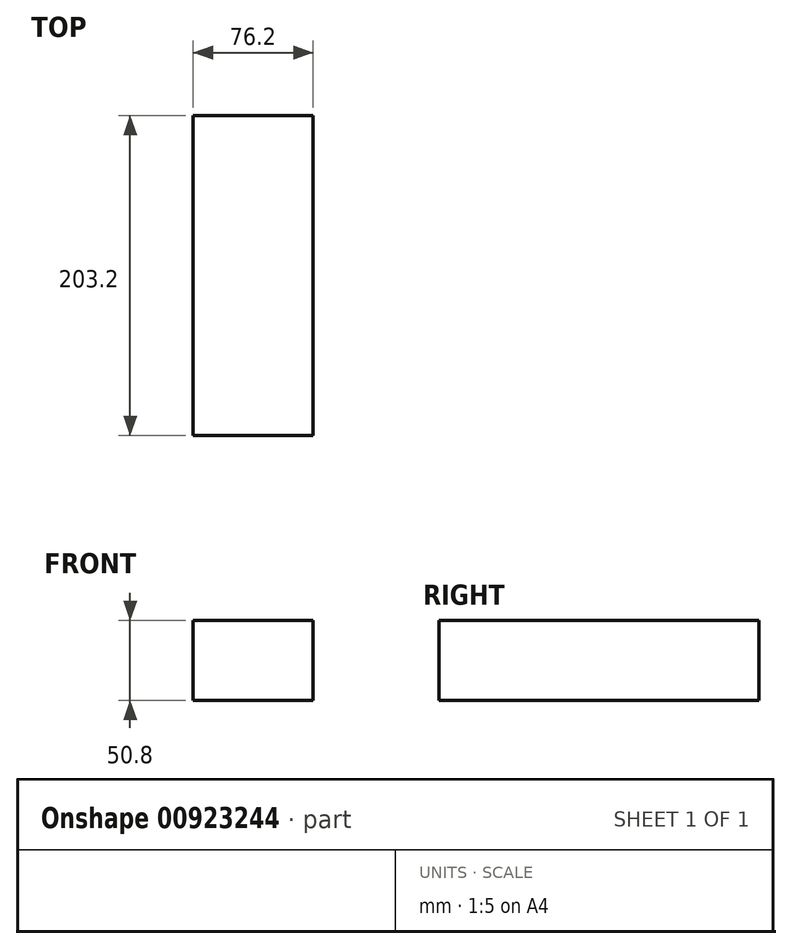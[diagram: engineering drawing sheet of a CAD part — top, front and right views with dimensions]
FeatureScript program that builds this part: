
annotation { "Feature Type Name" : "Feature", "Feature Type Description" : "" }
export const myFeature = defineFeature(function(context is Context, id is Id, definition is map)
    precondition{}
    {
        {
            var Q0;
            Q0=qCreatedBy(makeId("Top.planeOp"),FACE);
            var sketch = newSketch(context, id + "F0", { "sketchPlane" : qUnion([Q0])});
            skLineSegment(sketch, "E0.bottom", {"start": v(0, 0) * mm, "end": v(76.2, 0) * mm});
            skLineSegment(sketch, "E0.top", {"start": v(0, -203.2) * mm, "end": v(76.2, -203.2) * mm});
            skLineSegment(sketch, "E0.left", {"start": v(0, 0) * mm, "end": v(0, -203.2) * mm});
            skLineSegment(sketch, "E0.right", {"start": v(76.2, 0) * mm, "end": v(76.2, -203.2) * mm});
            skSolve(sketch);
        }
        {
            var Q0;
            Q0=makeQuery(id+"F0.imprint","IMPRINT",FACE,{"disambiguationData":[TD([[makeQuery(id+"F0.imprint","IMPRINT",EDGE,{"derivedFrom":sQuery(id+"F0.wireOp",EDGE,"E0.bottom")}),-1.0]])]});
            extrude(context, id + "F1", {"entities" : qUnion([Q0]), "depth" : 50.8 * mm, "offsetDistance" : 25.4 * mm});
        }
    });
